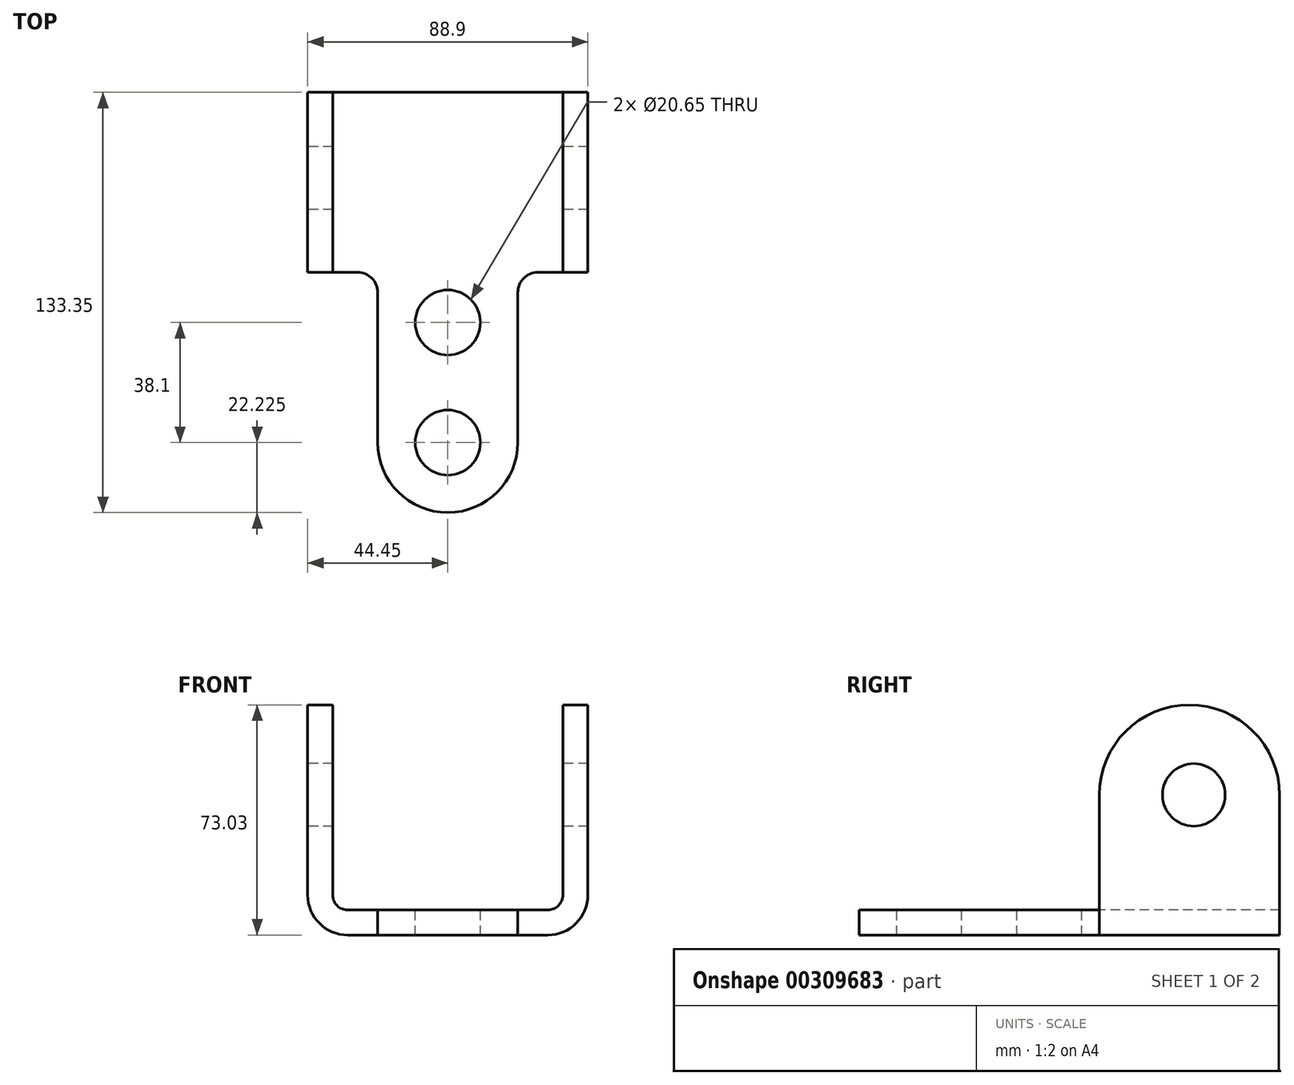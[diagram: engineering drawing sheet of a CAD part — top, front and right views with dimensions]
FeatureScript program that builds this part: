
annotation { "Feature Type Name" : "Feature", "Feature Type Description" : "" }
export const myFeature = defineFeature(function(context is Context, id is Id, definition is map)
    precondition{}
    {
        {
            var Q0;
            Q0=qCreatedBy(makeId("Front.planeOp"),FACE);
            var sketch = newSketch(context, id + "F0", { "sketchPlane" : qUnion([Q0])});
            skLineSegment(sketch, "E0", {"start": v(-31.75, 0) * mm, "end": v(31.75, 0) * mm});
            skLineSegment(sketch, "E1", {"start": v(44.45, 12.7) * mm, "end": v(44.45, 73.03) * mm});
            skLineSegment(sketch, "E2", {"start": v(44.45, 73.03) * mm, "end": v(36.51, 73.03) * mm});
            skLineSegment(sketch, "E3", {"start": v(36.51, 73.03) * mm, "end": v(36.51, 12.7) * mm});
            skLineSegment(sketch, "E4", {"start": v(31.75, 7.94) * mm, "end": v(-31.75, 7.94) * mm});
            skLineSegment(sketch, "E5", {"start": v(-36.51, 12.7) * mm, "end": v(-36.51, 73.03) * mm});
            skLineSegment(sketch, "E6", {"start": v(-36.51, 73.03) * mm, "end": v(-44.45, 73.03) * mm});
            skLineSegment(sketch, "E7", {"start": v(-44.45, 73.03) * mm, "end": v(-44.45, 12.7) * mm});
            skPoint(sketch, "E8.visualSharp", {"position": v(-44.45, 0) * mm});
            skArc(sketch, "E8.filletArc", {"start": v(-44.45, 12.7) * mm, "mid": v(-40.73, 3.72) * mm, "end": v(-31.75, 0) * mm});
            skPoint(sketch, "E9.visualSharp", {"position": v(44.45, 0) * mm});
            skArc(sketch, "E9.filletArc", {"start": v(31.75, 0) * mm, "mid": v(40.73, 3.72) * mm, "end": v(44.45, 12.7) * mm});
            skPoint(sketch, "E10.visualSharp", {"position": v(-36.51, 7.94) * mm});
            skArc(sketch, "E10.filletArc", {"start": v(-36.51, 12.7) * mm, "mid": v(-35.12, 9.33) * mm, "end": v(-31.75, 7.94) * mm});
            skPoint(sketch, "E11.visualSharp", {"position": v(36.51, 7.94) * mm});
            skArc(sketch, "E11.filletArc", {"start": v(31.75, 7.94) * mm, "mid": v(35.12, 9.33) * mm, "end": v(36.51, 12.7) * mm});
            skSolve(sketch);
        }
        {
            var Q0;
            Q0 = qSketchRegion(id + "F0", true);
            extrude(context, id + "F1", {"entities" : qUnion([Q0]), "oppositeDirection" : true, "depth" : 57.15 * mm});
        }
        {
            var Q0;
            Q0=makeQuery(id+"F1.opExtrude","CAP_EDGE",EDGE,{"disambiguationData":[OSD([sQuery(id+"F0.wireOp",EDGE,"E2")])],"isStart":true});
            var Q1;
            Q1=makeQuery(id+"F1.opExtrude","CAP_EDGE",EDGE,{"disambiguationData":[OSD([sQuery(id+"F0.wireOp",EDGE,"E2")])],"isStart":false});
            fillet(context, id + "F2", {"entities" : qUnion([Q0, Q1]), "radius" : 28.57 * mm, "tangentPropagation" : true, "allowEdgeOverflow" : false});
        }
        {
            var Q0;
            Q0=makeQuery(id+"F1.opExtrude","CAP_EDGE",EDGE,{"disambiguationData":[OSD([sQuery(id+"F0.wireOp",EDGE,"E6")])],"isStart":true});
            var Q1;
            Q1=makeQuery(id+"F1.opExtrude","CAP_EDGE",EDGE,{"disambiguationData":[OSD([sQuery(id+"F0.wireOp",EDGE,"E6")])],"isStart":false});
            fillet(context, id + "F3", {"entities" : qUnion([Q0, Q1]), "radius" : 28.57 * mm, "tangentPropagation" : true, "allowEdgeOverflow" : false});
        }
        {
            var Q0;
            Q0=makeQuery(id+"F1.opExtrude","SWEPT_FACE",FACE,{"disambiguationData":[OSD([sQuery(id+"F0.wireOp",EDGE,"E7")])]});
            var sketch = newSketch(context, id + "F4", { "sketchPlane" : qUnion([Q0])});
            skCircle(sketch, "E12", {"center": v(-29.96, 44.45) * mm, "radius": 9.92 * mm});
            skSolve(sketch);
        }
        {
            var Q0;
            Q0 = qSketchRegion(id + "F4", true);
            extrude(context, id + "F5", {"entities" : qUnion([Q0]), "operationType" : NewBodyOperationType.REMOVE, "endBound" : BoundingType.THROUGH_ALL, "oppositeDirection" : true, "depth" : 25.4 * mm});
        }
        {
            var Q0;
            Q0=makeQuery(id+"F1.opExtrude","SWEPT_FACE",FACE,{"disambiguationData":[OSD([sQuery(id+"F0.wireOp",EDGE,"E4")])]});
            var sketch = newSketch(context, id + "F6", { "sketchPlane" : qUnion([Q0])});
            skLineSegment(sketch, "E13", {"start": v(22.22, -6.35) * mm, "end": v(22.22, -53.98) * mm});
            skLineSegment(sketch, "E14", {"start": v(22.22, -53.98) * mm, "end": v(22.22, -6.35) * mm});
            skLineSegment(sketch, "E15", {"start": v(-22.23, -6.35) * mm, "end": v(-22.23, -53.98) * mm});
            skLineSegment(sketch, "E16", {"start": v(-22.23, -53.98) * mm, "end": v(-22.23, -6.35) * mm});
            skArc(sketch, "E17", {"start": v(-22.23, -53.98) * mm, "mid": v(0, -76.2) * mm, "end": v(22.23, -53.98) * mm});
            skLineSegment(sketch, "E18", {"start": v(22.22, 0) * mm, "end": v(-22.22, 0) * mm, "construction": true});
            skCircle(sketch, "E19", {"center": v(0, -15.88) * mm, "radius": 10.33 * mm});
            skCircle(sketch, "E20", {"center": v(0, -53.98) * mm, "radius": 10.33 * mm});
            skLineSegment(sketch, "E21", {"start": v(22.22, 0) * mm, "end": v(33.26, 0) * mm, "construction": true});
            skLineSegment(sketch, "E22", {"start": v(33.26, 0) * mm, "end": v(28.57, 0) * mm, "construction": true});
            skLineSegment(sketch, "E23", {"start": v(-28.58, 0) * mm, "end": v(-31.75, 0) * mm, "construction": true});
            skPoint(sketch, "E24.visualSharp", {"position": v(22.22, 0) * mm});
            skArc(sketch, "E24.filletArc", {"start": v(28.57, 0) * mm, "mid": v(24.08, -1.86) * mm, "end": v(22.22, -6.35) * mm});
            skPoint(sketch, "E25.visualSharp", {"position": v(-22.23, 0) * mm});
            skArc(sketch, "E25.filletArc", {"start": v(-22.23, -6.35) * mm, "mid": v(-24.08, -1.86) * mm, "end": v(-28.58, 0) * mm});
            skLineSegment(sketch, "E26", {"start": v(28.57, 0) * mm, "end": v(-28.58, 0) * mm, "construction": true});
            skLineSegment(sketch, "E27", {"start": v(28.57, 0) * mm, "end": v(-28.58, 0) * mm});
            skSolve(sketch);
        }
        {
            var Q0;
            Q0 = qSketchRegion(id + "F6", true);
            var Q1;
            Q1=makeQuery(id+"F1.opExtrude","SWEPT_FACE",FACE,{"disambiguationData":[OSD([sQuery(id+"F0.wireOp",EDGE,"E0")])]});
            extrude(context, id + "F7", {"entities" : qUnion([Q0]), "operationType" : NewBodyOperationType.ADD, "endBound" : BoundingType.UP_TO_SURFACE, "oppositeDirection" : true, "endBoundEntityFace" : qUnion([Q1]), "depth" : 25.4 * mm});
        }
    });
